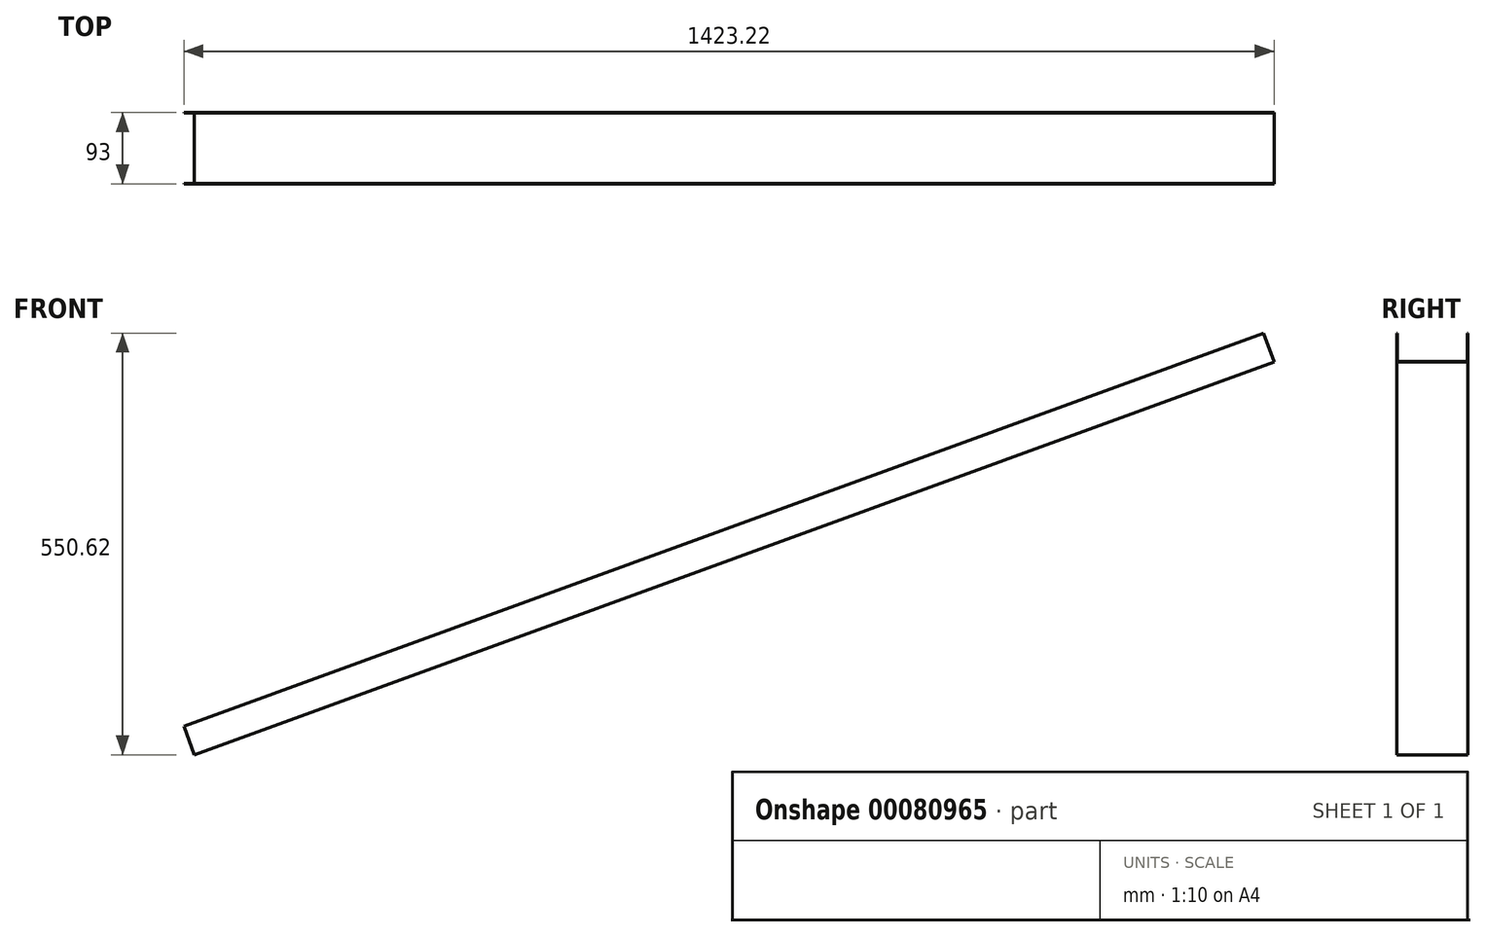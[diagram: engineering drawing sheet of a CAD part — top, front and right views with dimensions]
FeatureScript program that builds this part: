
annotation { "Feature Type Name" : "Feature", "Feature Type Description" : "" }
export const myFeature = defineFeature(function(context is Context, id is Id, definition is map)
    precondition{}
    {
        {
            var Q0;
            Q0=qCreatedBy(makeId("Right.planeOp"),FACE);
            var sketch = newSketch(context, id + "F0", { "sketchPlane" : qUnion([Q0])});
            skLineSegment(sketch, "E0.bottom", {"start": v(46.5, 20) * mm, "end": v(46, 20) * mm});
            skLineSegment(sketch, "E0.top", {"start": v(46.5, -20) * mm, "end": v(-46.5, -20) * mm});
            skLineSegment(sketch, "E0.left", {"start": v(46.5, 20) * mm, "end": v(46.5, -20) * mm});
            skLineSegment(sketch, "E0.right", {"start": v(-46.5, 20) * mm, "end": v(-46.5, -20) * mm});
            skPoint(sketch, "E0.middle", {"position": v(0, 0) * mm});
            skLineSegment(sketch, "E1.0", {"start": v(46, 19.5) * mm, "end": v(-46, 19.5) * mm, "construction": true});
            skLineSegment(sketch, "E1.1", {"start": v(46, 19.5) * mm, "end": v(46, -19.5) * mm});
            skLineSegment(sketch, "E1.2", {"start": v(46, -19.5) * mm, "end": v(-46, -19.5) * mm});
            skLineSegment(sketch, "E1.3", {"start": v(-46, 19.5) * mm, "end": v(-46, -19.5) * mm});
            skLineSegment(sketch, "E2", {"start": v(-46, 19.5) * mm, "end": v(-46, 20) * mm});
            skLineSegment(sketch, "E3", {"start": v(46, 19.5) * mm, "end": v(46, 20) * mm});
            skLineSegment(sketch, "E4.trimOffspring", {"start": v(-46, 20) * mm, "end": v(-46.5, 20) * mm});
            skSolve(sketch);
        }
        {
            var Q0;
            Q0=makeQuery(id+"F0.imprint","IMPRINT",FACE,{"disambiguationData":[TD([[makeQuery(id+"F0.imprint","IMPRINT",EDGE,{"derivedFrom":sQuery(id+"F0.wireOp",EDGE,"E0.bottom")}),1.0]])]});
            extrude(context, id + "F1", {"entities" : qUnion([Q0]), "depth" : 1500 * mm});
        }
        {
            var Q0;
            Q0=makeQuery(id+"F1.opExtrude","SWEPT_BODY",BODY,{"disambiguationData":[OSD([sQuery(id+"F0.wireOp",EDGE,"E0.bottom"),sQuery(id+"F0.wireOp",EDGE,"E0.top"),sQuery(id+"F0.wireOp",EDGE,"E0.left"),sQuery(id+"F0.wireOp",EDGE,"E0.right"),sQuery(id+"F0.wireOp",EDGE,"E1.1"),sQuery(id+"F0.wireOp",EDGE,"E1.2"),sQuery(id+"F0.wireOp",EDGE,"E1.3"),sQuery(id+"F0.wireOp",EDGE,"E2"),sQuery(id+"F0.wireOp",EDGE,"E3"),sQuery(id+"F0.wireOp",EDGE,"E4.trimOffspring")])]});
            var Q1;
            Q1=makeQuery(id+"F1.opExtrude","CAP_EDGE",EDGE,{"disambiguationData":[OSD([sQuery(id+"F0.wireOp",EDGE,"E1.2")])],"isStart":true});
            transform(context, id + "F2", {"entities" : qUnion([Q0]), "transformType" : TransformType.ROTATION, "transformAxis" : qUnion([Q1]), "angle" : 20 * degree, "makeCopy" : false});
        }
    });
